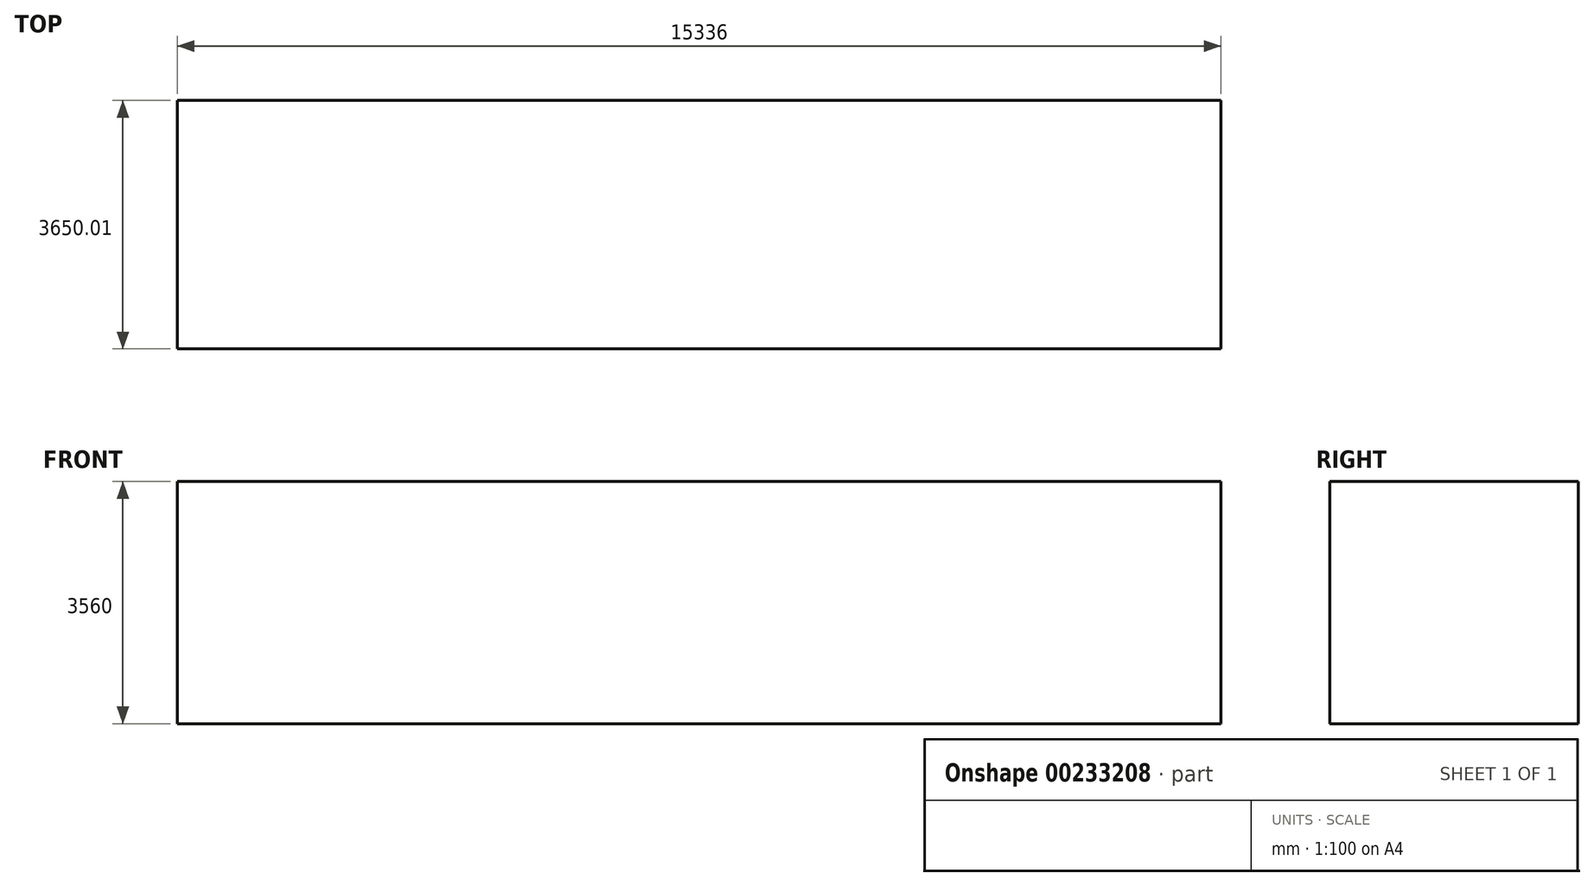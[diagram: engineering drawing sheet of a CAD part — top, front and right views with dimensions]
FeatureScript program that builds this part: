
annotation { "Feature Type Name" : "Feature", "Feature Type Description" : "" }
export const myFeature = defineFeature(function(context is Context, id is Id, definition is map)
    precondition{}
    {
        {
            var Q0;
            Q0=qCreatedBy(makeId("Top.planeOp"),FACE);
            var sketch = newSketch(context, id + "F0", { "sketchPlane" : qUnion([Q0])});
            skLineSegment(sketch, "E0.bottom", {"start": v(-7657.5, -5090.4) * mm, "end": v(7678.5, -5090.4) * mm});
            skLineSegment(sketch, "E0.top", {"start": v(-7657.5, -8740.4) * mm, "end": v(7678.5, -8740.4) * mm});
            skLineSegment(sketch, "E0.left", {"start": v(-7657.5, -5090.4) * mm, "end": v(-7657.5, -8740.4) * mm});
            skLineSegment(sketch, "E0.right", {"start": v(7678.5, -5090.4) * mm, "end": v(7678.5, -8740.4) * mm});
            skSolve(sketch);
        }
        {
            var Q0;
            Q0 = qSketchRegion(id + "F0", true);
            extrude(context, id + "F1", {"entities" : qUnion([Q0]), "depth" : 3560 * mm});
        }
    });
